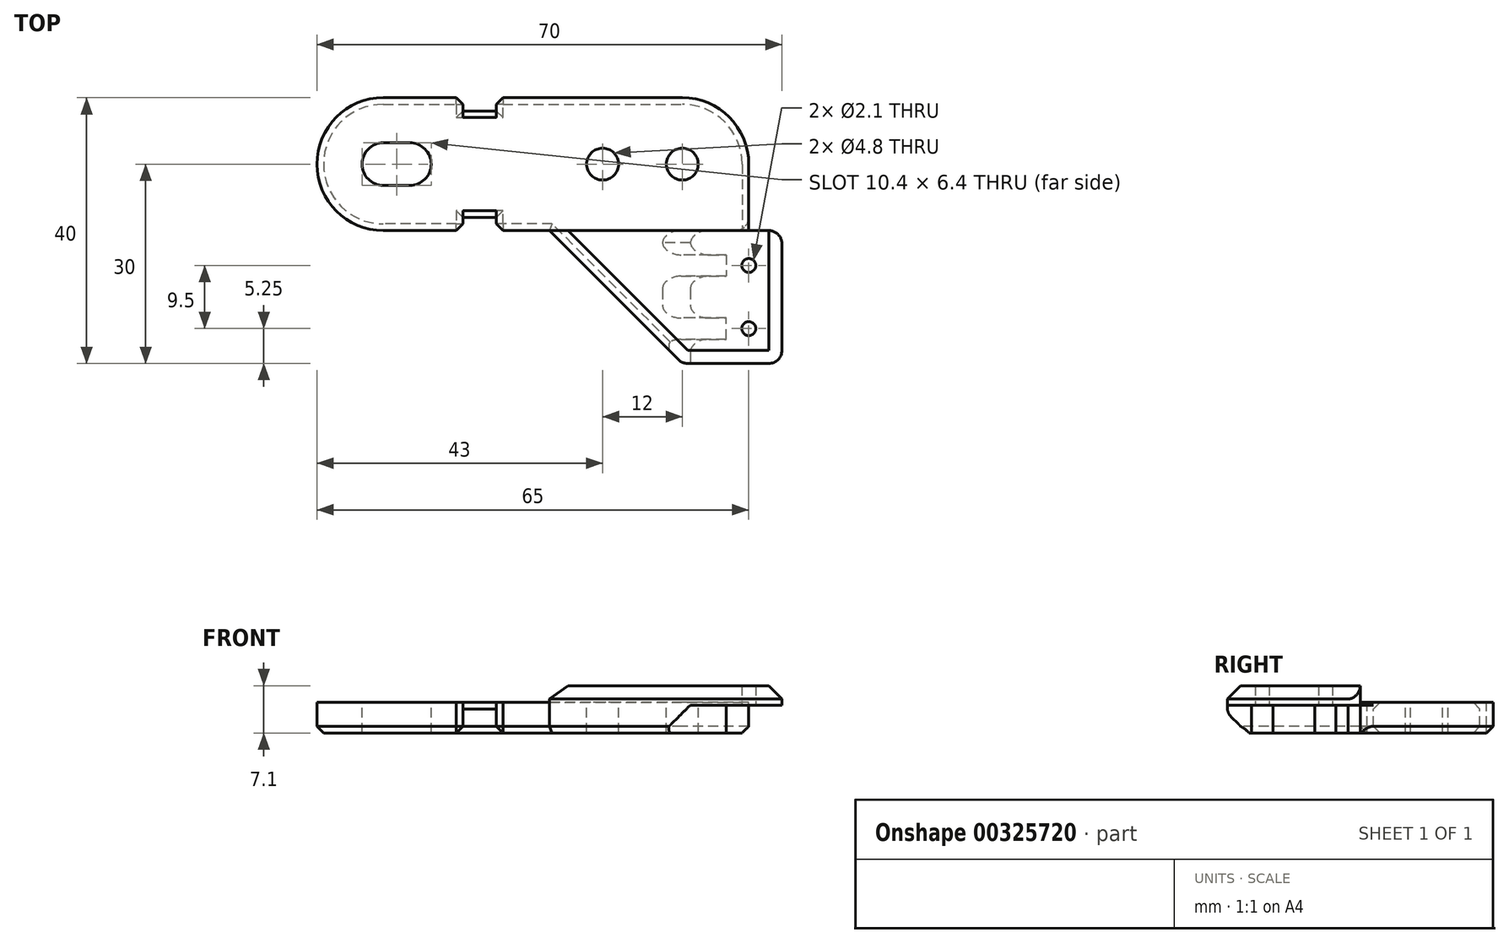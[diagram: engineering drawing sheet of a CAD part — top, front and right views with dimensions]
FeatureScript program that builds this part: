
annotation { "Feature Type Name" : "Feature", "Feature Type Description" : "" }
export const myFeature = defineFeature(function(context is Context, id is Id, definition is map)
    precondition{}
    {
        {
            var Q0;
            Q0=qCreatedBy(makeId("Top.planeOp"),FACE);
            var sketch = newSketch(context, id + "F0", { "sketchPlane" : qUnion([Q0])});
            skLineSegment(sketch, "E0.top", {"start": v(-25, -10) * mm, "end": v(-13, -10) * mm});
            skPoint(sketch, "E0.middle", {"position": v(0, 0) * mm});
            skArc(sketch, "E1", {"start": v(-25, 3.2) * mm, "mid": v(-28.2, 0) * mm, "end": v(-25, -3.2) * mm});
            skCircle(sketch, "E2", {"center": v(30, -15.25) * mm, "radius": 1.05 * mm});
            skCircle(sketch, "E3.MirrorC", {"center": v(30, -24.75) * mm, "radius": 1.05 * mm});
            skPoint(sketch, "E4.visualSharp", {"position": v(35, -10) * mm});
            skLineSegment(sketch, "E5", {"start": v(26.6, -23.15) * mm, "end": v(26.6, -26.35) * mm});
            skPoint(sketch, "E6", {"position": v(20, 0) * mm});
            skPoint(sketch, "E7", {"position": v(8, 0) * mm});
            skLineSegment(sketch, "E8", {"start": v(35, -12) * mm, "end": v(35, -28) * mm});
            skLineSegment(sketch, "E9", {"start": v(33, -30) * mm, "end": v(20.83, -30) * mm});
            skLineSegment(sketch, "E10", {"start": v(19.41, -29.41) * mm, "end": v(0, -10) * mm});
            skLineSegment(sketch, "E11", {"start": v(20, 10) * mm, "end": v(-8, 10) * mm});
            skPoint(sketch, "E12.visualSharp", {"position": v(35, -30) * mm});
            skArc(sketch, "E12.filletArc", {"start": v(33, -30) * mm, "mid": v(34.41, -29.41) * mm, "end": v(35, -28) * mm});
            skArc(sketch, "E13.filletArc", {"start": v(35, -12) * mm, "mid": v(34.41, -10.59) * mm, "end": v(33, -10) * mm});
            skPoint(sketch, "E14.visualSharp", {"position": v(20, -30) * mm});
            skArc(sketch, "E14.filletArc", {"start": v(19.41, -29.41) * mm, "mid": v(20.06, -29.85) * mm, "end": v(20.83, -30) * mm});
            skLineSegment(sketch, "E15", {"start": v(35, -20) * mm, "end": v(26.6, -20) * mm, "construction": true});
            skLineSegment(sketch, "E16", {"start": v(0, -10) * mm, "end": v(33, -10) * mm});
            skArc(sketch, "E17", {"start": v(-25, -10) * mm, "mid": v(-35, 0) * mm, "end": v(-25, 10) * mm});
            skCircle(sketch, "E18", {"center": v(20, 0) * mm, "radius": 10 * mm, "construction": true});
            skPoint(sketch, "E19.newPointB", {"position": v(20, 10) * mm});
            skLineSegment(sketch, "E20.bottom", {"start": v(26.6, -23.15) * mm, "end": v(21.6, -23.15) * mm});
            skLineSegment(sketch, "E20.top", {"start": v(26.6, -26.35) * mm, "end": v(21.6, -26.35) * mm});
            skPoint(sketch, "E20.middle", {"position": v(19.88, -24.75) * mm});
            skLineSegment(sketch, "E21.bottom", {"start": v(26.6, -16.85) * mm, "end": v(21.6, -16.85) * mm});
            skLineSegment(sketch, "E21.top", {"start": v(26.6, -13.65) * mm, "end": v(21.6, -13.65) * mm});
            skLineSegment(sketch, "E21.left", {"start": v(26.6, -16.85) * mm, "end": v(26.6, -13.65) * mm});
            skPoint(sketch, "E21.middle", {"position": v(15.13, -15.25) * mm});
            skPoint(sketch, "E20.right.end.orphan", {"position": v(13.15, -26.35) * mm});
            skPoint(sketch, "E21.right.start.orphan", {"position": v(3.65, -16.85) * mm});
            skLineSegment(sketch, "E22", {"start": v(21.6, -10) * mm, "end": v(21.6, -13.65) * mm});
            skLineSegment(sketch, "E23.trimOffspring", {"start": v(21.6, -26.35) * mm, "end": v(21.6, -31.6) * mm});
            skLineSegment(sketch, "E24.trimOffspring", {"start": v(21.6, -16.85) * mm, "end": v(21.6, -23.15) * mm});
            skPoint(sketch, "E25.orphan", {"position": v(13.15, -23.15) * mm});
            skPoint(sketch, "E26.orphan", {"position": v(26.6, -30) * mm});
            skLineSegment(sketch, "E27.trimOffspring", {"start": v(26.6, -13.65) * mm, "end": v(26.6, -16.85) * mm});
            skPoint(sketch, "E28.orphan", {"position": v(3.65, -13.65) * mm});
            skLineSegment(sketch, "E29", {"start": v(30, -10) * mm, "end": v(30, 0) * mm});
            skArc(sketch, "E30", {"start": v(20, 10) * mm, "mid": v(27.07, 7.07) * mm, "end": v(30, 0) * mm});
            skLineSegment(sketch, "E31.top", {"start": v(-8, -8) * mm, "end": v(-13, -8) * mm});
            skLineSegment(sketch, "E31.left", {"start": v(-8, -10) * mm, "end": v(-8, -8) * mm});
            skLineSegment(sketch, "E31.right", {"start": v(-13, -10) * mm, "end": v(-13, -8) * mm});
            skLineSegment(sketch, "E32", {"start": v(-8, -10) * mm, "end": v(0, -10) * mm});
            skLineSegment(sketch, "E33.MirrorCS", {"start": v(-8, 10) * mm, "end": v(-8, 8) * mm});
            skLineSegment(sketch, "E34.MirrorCS", {"start": v(-13, 10) * mm, "end": v(-13, 8) * mm});
            skLineSegment(sketch, "E35.MirrorCS", {"start": v(-8, 8) * mm, "end": v(-13, 8) * mm});
            skLineSegment(sketch, "E36.trimOffspring", {"start": v(-13, 10) * mm, "end": v(-25, 10) * mm});
            skArc(sketch, "E37", {"start": v(-21, -3.2) * mm, "mid": v(-17.8, 0) * mm, "end": v(-21, 3.2) * mm});
            skLineSegment(sketch, "E38", {"start": v(-21, -3.2) * mm, "end": v(-25, -3.2) * mm});
            skLineSegment(sketch, "E39", {"start": v(-21, 3.2) * mm, "end": v(-25, 3.2) * mm});
            skSolve(sketch);
        }
        {
            var Q0;
            {var subQ2=sQuery(id+"F0.wireOp",EDGE,"E5");Q0=makeQuery(id+"F0.imprint","IMPRINT",FACE,{"disambiguationData":[TD([[makeQuery(id+"F0.imprint","IMPRINT",EDGE,{"derivedFrom":subQ2}),-1.0]])]});}
            var Q1;
            {var subQ1=sQuery(id+"F0.wireOp",EDGE,"c53eef99-03b7-40e2-be4a-50fc72cb1684.filletArc");Q1=makeQuery(id+"F0.imprint","IMPRINT",FACE,{"disambiguationData":[TD([[makeQuery(id+"F0.imprint","IMPRINT",EDGE,{"derivedFrom":subQ1}),-1.0]])]});}
            var Q2;
            {var subQ6=sQuery(id+"F0.wireOp",EDGE,"E10");Q2=makeQuery(id+"F0.imprint","IMPRINT",FACE,{"disambiguationData":[TD([[makeQuery(id+"F0.imprint","IMPRINT",EDGE,{"derivedFrom":subQ6}),-1.0]])]});}
            extrude(context, id + "F1", {"entities" : qUnion([Q0, Q1, Q2]), "oppositeDirection" : true, "depth" : 4.6 * mm});
        }
        {
            var Q0;
            {var subQ2=sQuery(id+"F0.wireOp",EDGE,"E5");Q0=makeQuery(id+"F0.imprint","IMPRINT",FACE,{"disambiguationData":[TD([[makeQuery(id+"F0.imprint","IMPRINT",EDGE,{"derivedFrom":subQ2}),-1.0]])]});}
            var Q1;
            Q1=makeQuery(id+"F0.imprint","IMPRINT",FACE,{"disambiguationData":[TD([[makeQuery(id+"F0.imprint","IMPRINT",EDGE,{"derivedFrom":sQuery(id+"F0.wireOp",EDGE,"E2")}),-1.0]])]});
            var Q2;
            {var subQ0=sQuery(id+"F0.wireOp",EDGE,"E21.bottom");Q2=makeQuery(id+"F0.imprint","IMPRINT",FACE,{"disambiguationData":[TD([[makeQuery(id+"F0.imprint","IMPRINT",EDGE,{"derivedFrom":subQ0}),-1.0]])]});}
            var Q3;
            {var subQ0=sQuery(id+"F0.wireOp",EDGE,"E20.bottom");Q3=makeQuery(id+"F0.imprint","IMPRINT",FACE,{"disambiguationData":[TD([[makeQuery(id+"F0.imprint","IMPRINT",EDGE,{"derivedFrom":subQ0}),1.0]])]});}
            var Q4;
            {var subQ0=sQuery(id+"F0.wireOp",EDGE,"E14.filletArc");Q4=makeQuery(id+"F0.imprint","IMPRINT",FACE,{"disambiguationData":[TD([[makeQuery(id+"F0.imprint","IMPRINT",EDGE,{"derivedFrom":subQ0}),1.0]])]});}
            var Q5;
            {var subQ1=sQuery(id+"F0.wireOp",EDGE,"c53eef99-03b7-40e2-be4a-50fc72cb1684.filletArc");Q5=makeQuery(id+"F0.imprint","IMPRINT",FACE,{"disambiguationData":[TD([[makeQuery(id+"F0.imprint","IMPRINT",EDGE,{"derivedFrom":subQ1}),-1.0]])]});}
            extrude(context, id + "F2", {"entities" : qUnion([Q0, Q1, Q2, Q3, Q4, Q5]), "operationType" : NewBodyOperationType.ADD, "depth" : 2.5 * mm, "hasSecondDirection" : true, "secondDirectionOppositeDirection" : true, "secondDirectionDepth" : 0.4 * mm});
        }
        {
            var Q0;
            Q0=makeQuery(id+"F1.opExtrude","CAP_EDGE",EDGE,{"disambiguationData":[OSD([sQuery(id+"F0.wireOp",EDGE,"E24.trimOffspring")])],"isStart":false});
            var Q1;
            Q1=makeQuery(id+"F1.opExtrude","CAP_EDGE",EDGE,{"disambiguationData":[OSD([sQuery(id+"F0.wireOp",EDGE,"E22")])],"isStart":false});
            var Q2;
            Q2=makeQuery(id+"F1.opExtrude","CAP_EDGE",EDGE,{"disambiguationData":[OSD([sQuery(id+"F0.wireOp",EDGE,"E23.trimOffspring")])],"isStart":false});
            chamfer(context, id + "F3", {"entities" : qUnion([Q0, Q1, Q2]), "width" : 4.6 * mm});
        }
        {
            var Q0;
            Q0=makeQuery(id+"F2.opExtrude","CAP_EDGE",EDGE,{"disambiguationData":[OSD([sQuery(id+"F0.wireOp",EDGE,"E10")])],"isStart":false});
            var Q1;
            Q1=makeQuery(id+"F2.opExtrude","CAP_EDGE",EDGE,{"disambiguationData":[OSD([sQuery(id+"F0.wireOp",EDGE,"E9")])],"isStart":false});
            var Q2;
            Q2=makeQuery(id+"F2.opExtrude","CAP_EDGE",EDGE,{"disambiguationData":[OSD([sQuery(id+"F0.wireOp",EDGE,"E8")])],"isStart":false});
            var Q3;
            Q3=makeQuery(id+"F2.opExtrude","CAP_EDGE",EDGE,{"disambiguationData":[OSD([sQuery(id+"F0.wireOp",EDGE,"E13.filletArc")])],"isStart":false});
            chamfer(context, id + "F4", {"entities" : qUnion([Q0, Q1, Q2, Q3]), "width" : 2 * mm});
        }
        {
            var Q0;
            {var subQ1=sQuery(id+"F0.wireOp",EDGE,"E0.top");Q0=makeQuery(id+"F0.imprint","IMPRINT",FACE,{"disambiguationData":[TD([[makeQuery(id+"F0.imprint","IMPRINT",EDGE,{"derivedFrom":subQ1}),1.0]])]});}
            var Q1;
            Q1=makeQuery(id+"F1.opExtrude","CAP_FACE",FACE,{"disambiguationData":[OSD([sQuery(id+"F0.wireOp",EDGE,"E9"),sQuery(id+"F0.wireOp",EDGE,"E10"),sQuery(id+"F0.wireOp",EDGE,"E14.filletArc"),sQuery(id+"F0.wireOp",EDGE,"E16"),sQuery(id+"F0.wireOp",EDGE,"E20.bottom"),sQuery(id+"F0.wireOp",EDGE,"E20.top"),sQuery(id+"F0.wireOp",EDGE,"E5"),sQuery(id+"F0.wireOp",EDGE,"E21.bottom"),sQuery(id+"F0.wireOp",EDGE,"E21.top"),sQuery(id+"F0.wireOp",EDGE,"E22"),sQuery(id+"F0.wireOp",EDGE,"E23.trimOffspring"),sQuery(id+"F0.wireOp",EDGE,"E24.trimOffspring"),sQuery(id+"F0.wireOp",EDGE,"E27.trimOffspring")])],"isStart":false});
            extrude(context, id + "F5", {"entities" : qUnion([Q0]), "operationType" : NewBodyOperationType.ADD, "endBound" : BoundingType.UP_TO_SURFACE, "oppositeDirection" : true, "endBoundEntityFace" : qUnion([Q1]), "depth" : 25 * mm});
        }
        {
            var Q0;
            Q0=sQuery(id+"F0.wireOp",VERTEX,"E6");
            var Q1;
            Q1=sQuery(id+"F0.wireOp",VERTEX,"E7");
            var Q2;
            Q2=makeQuery(id+"F1.opExtrude","SWEPT_BODY",BODY,{"disambiguationData":[OSD([sQuery(id+"F0.wireOp",EDGE,"E9"),sQuery(id+"F0.wireOp",EDGE,"E10"),sQuery(id+"F0.wireOp",EDGE,"E14.filletArc"),sQuery(id+"F0.wireOp",EDGE,"E16"),sQuery(id+"F0.wireOp",EDGE,"E20.bottom"),sQuery(id+"F0.wireOp",EDGE,"E20.top"),sQuery(id+"F0.wireOp",EDGE,"E5"),sQuery(id+"F0.wireOp",EDGE,"E21.bottom"),sQuery(id+"F0.wireOp",EDGE,"E21.top"),sQuery(id+"F0.wireOp",EDGE,"E22"),sQuery(id+"F0.wireOp",EDGE,"E23.trimOffspring"),sQuery(id+"F0.wireOp",EDGE,"E24.trimOffspring"),sQuery(id+"F0.wireOp",EDGE,"E27.trimOffspring")])]});
            hole(context, id + "F6", {"style" : HoleStyle.SIMPLE, "endStyle" : HoleEndStyle.BLIND, "holeDiameter" : 4.8 * mm, "holeDepth" : 14.25 * mm, "tappedDepth" : 12 * mm, "tapClearance" : 3, "startFromSketch" : true, "locations" : qUnion([Q0, Q1]), "scope" : qUnion([Q2])});
        }
        {
            var Q0;
            Q0=makeQuery(id+"F3.opChamfer","BLEND_EDGE",EDGE,{"blendedFrom":[makeQuery(id+"F1.opExtrude","CAP_EDGE",EDGE,{"disambiguationData":[OSD([sQuery(id+"F0.wireOp",EDGE,"E24.trimOffspring")])],"isStart":false}),makeQuery(id+"F1.opExtrude","SWEPT_FACE",FACE,{"disambiguationData":[OSD([sQuery(id+"F0.wireOp",EDGE,"E20.bottom")])]})],"blendedInto":[makeQuery(id+"F1.opExtrude","SWEPT_FACE",FACE,{"disambiguationData":[OSD([sQuery(id+"F0.wireOp",EDGE,"E20.bottom")])]})]});
            var Q1;
            Q1=makeQuery(id+"F3.opChamfer","BLEND_EDGE",EDGE,{"blendedFrom":[makeQuery(id+"F1.opExtrude","CAP_EDGE",EDGE,{"disambiguationData":[OSD([sQuery(id+"F0.wireOp",EDGE,"E22")])],"isStart":false}),makeQuery(id+"F1.opExtrude","SWEPT_FACE",FACE,{"disambiguationData":[OSD([sQuery(id+"F0.wireOp",EDGE,"E21.top")])]})],"blendedInto":[makeQuery(id+"F1.opExtrude","SWEPT_FACE",FACE,{"disambiguationData":[OSD([sQuery(id+"F0.wireOp",EDGE,"E21.top")])]})]});
            var Q2;
            Q2=makeQuery(id+"F3.opChamfer","BLEND_EDGE",EDGE,{"blendedFrom":[makeQuery(id+"F1.opExtrude","CAP_EDGE",EDGE,{"disambiguationData":[OSD([sQuery(id+"F0.wireOp",EDGE,"E24.trimOffspring")])],"isStart":false}),makeQuery(id+"F1.opExtrude","SWEPT_FACE",FACE,{"disambiguationData":[OSD([sQuery(id+"F0.wireOp",EDGE,"E21.bottom")])]})],"blendedInto":[makeQuery(id+"F1.opExtrude","SWEPT_FACE",FACE,{"disambiguationData":[OSD([sQuery(id+"F0.wireOp",EDGE,"E21.bottom")])]})]});
            var Q3;
            {var subQ0=sQuery(id+"F0.wireOp",EDGE,"E16");Q3=makeQuery(id+"F3.opChamfer","BLEND_EDGE",EDGE,{"blendedFrom":[makeQuery(id+"F1.opExtrude","CAP_EDGE",EDGE,{"disambiguationData":[OSD([sQuery(id+"F0.wireOp",EDGE,"E22")])],"isStart":false}),makeQuery(id+"F2.boolean.opBoolean","MERGE",FACE,{"derivedFrom":[makeQuery(id+"F1.opExtrude","SWEPT_FACE",FACE,{"disambiguationData":[OSD([subQ0])]}),makeQuery(id+"F2.opExtrude","SWEPT_FACE",FACE,{"disambiguationData":[OSD([subQ0])]})]})],"blendedInto":[makeQuery(id+"F2.boolean.opBoolean","MERGE",FACE,{"derivedFrom":[makeQuery(id+"F1.opExtrude","SWEPT_FACE",FACE,{"disambiguationData":[OSD([subQ0])]}),makeQuery(id+"F2.opExtrude","SWEPT_FACE",FACE,{"disambiguationData":[OSD([subQ0])]})]})]});}
            var Q4;
            Q4=makeQuery(id+"F3.opChamfer","BLEND_EDGE",EDGE,{"blendedFrom":[makeQuery(id+"F1.opExtrude","CAP_EDGE",EDGE,{"disambiguationData":[OSD([sQuery(id+"F0.wireOp",EDGE,"E23.trimOffspring")])],"isStart":false}),makeQuery(id+"F1.opExtrude","SWEPT_FACE",FACE,{"disambiguationData":[OSD([sQuery(id+"F0.wireOp",EDGE,"E20.top")])]})],"blendedInto":[makeQuery(id+"F1.opExtrude","SWEPT_FACE",FACE,{"disambiguationData":[OSD([sQuery(id+"F0.wireOp",EDGE,"E20.top")])]})]});
            var Q5;
            {var subQ0=sQuery(id+"F0.wireOp",EDGE,"E16");var subQ1=sQuery(id+"F0.wireOp",EDGE,"E29");Q5=makeQuery(id+"F5.boolean.opBoolean","SPLIT",EDGE,{"disambiguationData":[topologyDisambiguationEdgeConnected([makeQuery(id+"F5.opExtrude","SWEPT_FACE",FACE,{"disambiguationData":[OSD([subQ0,sQuery(id+"F0.wireOp",EDGE,"E32")])]})])],"derivedFrom":makeQuery(id+"F5.opExtrude","SWEPT_EDGE",EDGE,{"disambiguationData":[OSD([subQ0,subQ1])]})});}
            fillet(context, id + "F7", {"entities" : qUnion([Q0, Q1, Q2, Q3, Q4, Q5]), "radius" : 2 * mm, "tangentPropagation" : true, "allowEdgeOverflow" : false});
        }
        {
            var Q0;
            Q0=makeQuery(id+"F1.opExtrude","CAP_EDGE",EDGE,{"disambiguationData":[OSD([sQuery(id+"F0.wireOp",EDGE,"E10")])],"isStart":false});
            var Q1;
            Q1=makeQuery(id+"F1.opExtrude","CAP_EDGE",EDGE,{"disambiguationData":[OSD([sQuery(id+"F0.wireOp",EDGE,"E5")])],"isStart":false});
            var Q2;
            Q2=makeQuery(id+"F1.opExtrude","CAP_EDGE",EDGE,{"disambiguationData":[OSD([sQuery(id+"F0.wireOp",EDGE,"E27.trimOffspring")])],"isStart":false});
            var Q3;
            Q3=makeQuery(id+"F5.opExtrude","CAP_EDGE",EDGE,{"disambiguationData":[OSD([sQuery(id+"F0.wireOp",EDGE,"E0.top")])],"isStart":false});
            var Q4;
            {var subQ0=sQuery(id+"F0.wireOp",EDGE,"E10");var subQ1=sQuery(id+"F0.wireOp",EDGE,"E32");var subQ2=sQuery(id+"F0.wireOp",EDGE,"E16");Q4=makeQuery(id+"F5.boolean.opBoolean","SPLIT",EDGE,{"disambiguationData":[TD([makeQuery(id+"F1.opExtrude","SWEPT_FACE",FACE,{"disambiguationData":[OSD([subQ0])]})])],"derivedFrom":makeQuery(id+"F5.opExtrude","CAP_EDGE",EDGE,{"disambiguationData":[OSD([subQ2,subQ1])],"isStart":false})});}
            var Q5;
            Q5=makeQuery(id+"F5.opExtrude","CAP_EDGE",EDGE,{"disambiguationData":[OSD([sQuery(id+"F0.wireOp",EDGE,"E31.top")])],"isStart":false});
            var Q6;
            Q6=makeQuery(id+"F5.opExtrude","CAP_EDGE",EDGE,{"disambiguationData":[OSD([sQuery(id+"F0.wireOp",EDGE,"E31.top")])],"isStart":true});
            var Q7;
            Q7=makeQuery(id+"F5.opExtrude","CAP_EDGE",EDGE,{"disambiguationData":[OSD([sQuery(id+"F0.wireOp",EDGE,"E35.MirrorCS")])],"isStart":false});
            var Q8;
            Q8=makeQuery(id+"F5.opExtrude","CAP_EDGE",EDGE,{"disambiguationData":[OSD([sQuery(id+"F0.wireOp",EDGE,"E35.MirrorCS")])],"isStart":true});
            var Q9;
            Q9=makeQuery(id+"F5.opExtrude","CAP_EDGE",EDGE,{"disambiguationData":[OSD([sQuery(id+"F0.wireOp",EDGE,"E11")])],"isStart":false});
            var Q10;
            {var subQ0=sQuery(id+"F0.wireOp",EDGE,"E10");var subQ1=sQuery(id+"F0.wireOp",EDGE,"E32");var subQ2=sQuery(id+"F0.wireOp",EDGE,"E16");Q10=makeQuery(id+"F5.boolean.opBoolean","SPLIT",EDGE,{"disambiguationData":[TD([makeQuery(id+"F1.opExtrude","SWEPT_FACE",FACE,{"disambiguationData":[OSD([subQ0])]})])],"derivedFrom":makeQuery(id+"F5.opExtrude","CAP_EDGE",EDGE,{"disambiguationData":[OSD([subQ2,subQ1])],"isStart":false})});}
            var Q11;
            Q11=makeQuery(id+"F5.opExtrude","SWEPT_EDGE",EDGE,{"disambiguationData":[OSD([sQuery(id+"F0.wireOp",EDGE,"E31.left"),sQuery(id+"F0.wireOp",EDGE,"E32")])]});
            var Q12;
            Q12=makeQuery(id+"F5.opExtrude","SWEPT_EDGE",EDGE,{"disambiguationData":[OSD([sQuery(id+"F0.wireOp",EDGE,"E0.top"),sQuery(id+"F0.wireOp",EDGE,"E31.right")])]});
            var Q13;
            Q13=makeQuery(id+"F5.opExtrude","SWEPT_EDGE",EDGE,{"disambiguationData":[OSD([sQuery(id+"F0.wireOp",EDGE,"E11"),sQuery(id+"F0.wireOp",EDGE,"E33.MirrorCS")])]});
            var Q14;
            Q14=makeQuery(id+"F5.opExtrude","SWEPT_EDGE",EDGE,{"disambiguationData":[OSD([sQuery(id+"F0.wireOp",EDGE,"E34.MirrorCS"),sQuery(id+"F0.wireOp",EDGE,"E36.trimOffspring")])]});
            var Q15;
            Q15=makeQuery(id+"F5.opExtrude","CAP_EDGE",EDGE,{"disambiguationData":[OSD([sQuery(id+"F0.wireOp",EDGE,"E33.MirrorCS")])],"isStart":false});
            var Q16;
            Q16=makeQuery(id+"F5.opExtrude","CAP_EDGE",EDGE,{"disambiguationData":[OSD([sQuery(id+"F0.wireOp",EDGE,"E34.MirrorCS")])],"isStart":false});
            var Q17;
            Q17=makeQuery(id+"F5.opExtrude","CAP_EDGE",EDGE,{"disambiguationData":[OSD([sQuery(id+"F0.wireOp",EDGE,"E31.left")])],"isStart":false});
            var Q18;
            Q18=makeQuery(id+"F5.opExtrude","CAP_EDGE",EDGE,{"disambiguationData":[OSD([sQuery(id+"F0.wireOp",EDGE,"E31.right")])],"isStart":false});
            var Q19;
            Q19=makeQuery(id+"F5.opExtrude","CAP_EDGE",EDGE,{"disambiguationData":[OSD([sQuery(id+"F0.wireOp",EDGE,"E29")])],"isStart":false});
            var Q20;
            Q20=makeQuery(id+"F5.opExtrude","CAP_EDGE",EDGE,{"disambiguationData":[OSD([sQuery(id+"F0.wireOp",EDGE,"E30")])],"isStart":false});
            var Q21;
            Q21=makeQuery(id+"F5.opExtrude","CAP_EDGE",EDGE,{"disambiguationData":[OSD([sQuery(id+"F0.wireOp",EDGE,"E36.trimOffspring")])],"isStart":false});
            var Q22;
            Q22=makeQuery(id+"F5.opExtrude","CAP_EDGE",EDGE,{"disambiguationData":[OSD([sQuery(id+"F0.wireOp",EDGE,"E17")])],"isStart":false});
            chamfer(context, id + "F8", {"entities" : qUnion([Q0, Q1, Q2, Q3, Q4, Q5, Q6, Q7, Q8, Q9, Q10, Q11, Q12, Q13, Q14, Q15, Q16, Q17, Q18, Q19, Q20, Q21, Q22]), "width" : 1 * mm});
        }
    });
